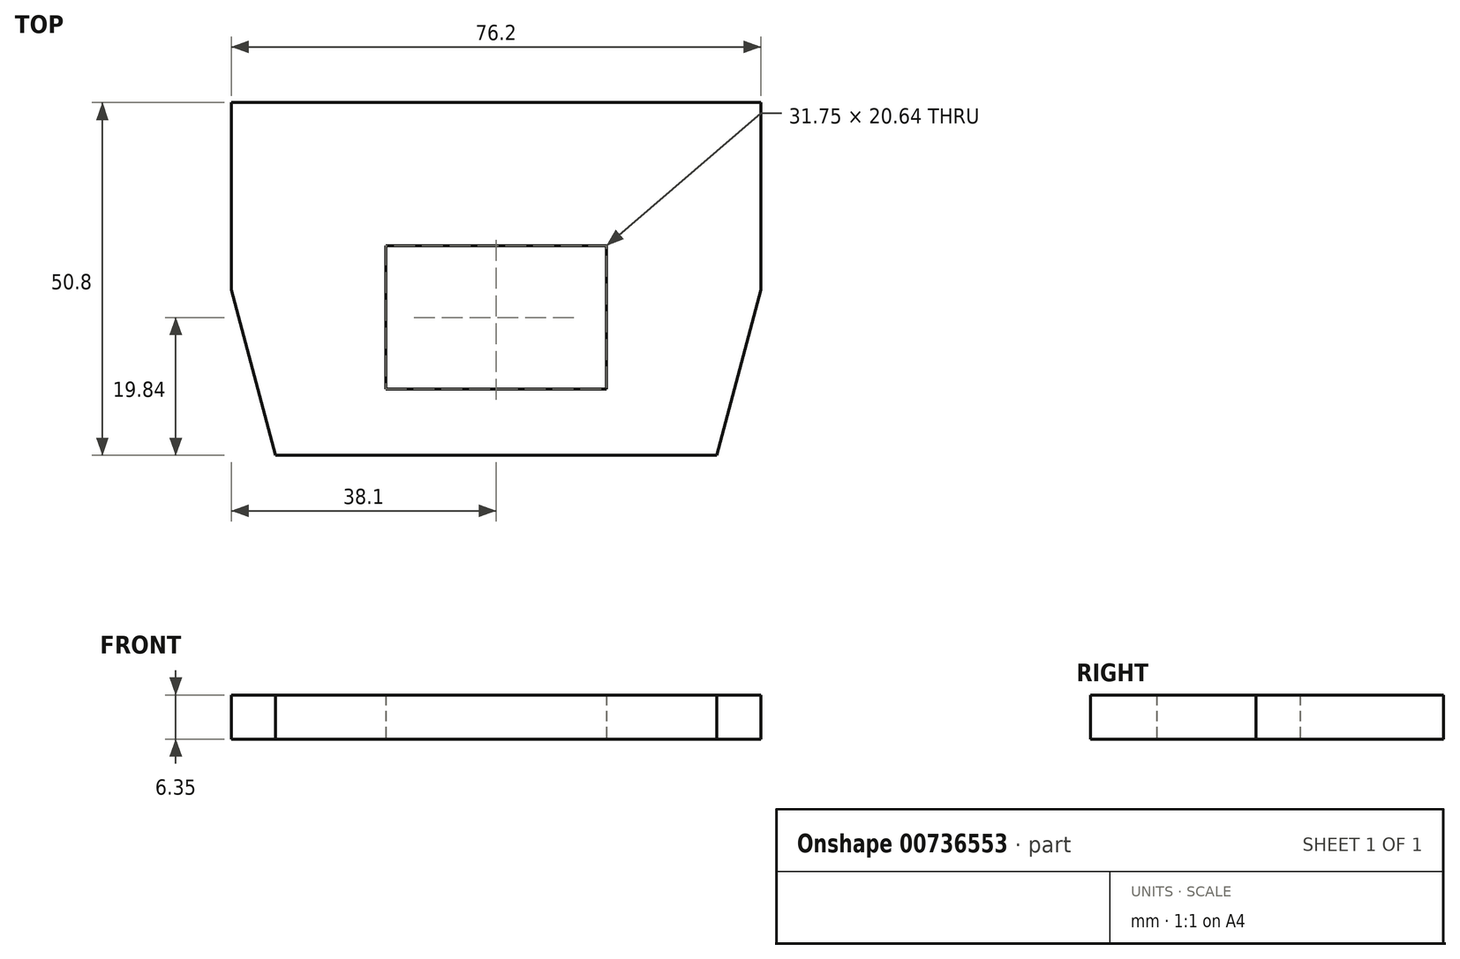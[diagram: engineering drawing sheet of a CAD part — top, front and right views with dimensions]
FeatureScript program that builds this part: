
annotation { "Feature Type Name" : "Feature", "Feature Type Description" : "" }
export const myFeature = defineFeature(function(context is Context, id is Id, definition is map)
    precondition{}
    {
        {
            var Q0;
            Q0=qCreatedBy(makeId("Top.planeOp"),FACE);
            var sketch = newSketch(context, id + "F0", { "sketchPlane" : qUnion([Q0])});
            skLineSegment(sketch, "E0", {"start": v(-75.44, 0) * mm, "end": v(76.77, 0) * mm, "construction": true});
            skLineSegment(sketch, "E1", {"start": v(0, 73.43) * mm, "end": v(0, -67) * mm, "construction": true});
            skLineSegment(sketch, "E2.0", {"start": v(38.1, 30.96) * mm, "end": v(38.1, 3.97) * mm});
            skLineSegment(sketch, "E3.0", {"start": v(0, 10.32) * mm, "end": v(15.88, 10.32) * mm});
            skLineSegment(sketch, "E4.0", {"start": v(0, -10.32) * mm, "end": v(15.88, -10.32) * mm});
            skLineSegment(sketch, "E5.0", {"start": v(0, -19.84) * mm, "end": v(31.75, -19.84) * mm});
            skLineSegment(sketch, "E6.0", {"start": v(0, 30.96) * mm, "end": v(38.1, 30.96) * mm});
            skLineSegment(sketch, "E7.0", {"start": v(-75.44, 3.97) * mm, "end": v(76.77, 3.97) * mm, "construction": true});
            skLineSegment(sketch, "E8", {"start": v(31.75, -19.84) * mm, "end": v(38.1, 3.97) * mm});
            skLineSegment(sketch, "E9.trimOffspring", {"start": v(15.88, 10.32) * mm, "end": v(15.88, -10.32) * mm});
            skLineSegment(sketch, "E10.MirrorCS", {"start": v(0, 30.96) * mm, "end": v(-38.1, 30.96) * mm});
            skLineSegment(sketch, "E11.MirrorCS", {"start": v(-38.1, 30.96) * mm, "end": v(-38.1, 3.97) * mm});
            skLineSegment(sketch, "E12.MirrorCS", {"start": v(-31.75, -19.84) * mm, "end": v(-38.1, 3.97) * mm});
            skLineSegment(sketch, "E13.MirrorCS", {"start": v(0, -19.84) * mm, "end": v(-31.75, -19.84) * mm});
            skLineSegment(sketch, "E14.MirrorCS", {"start": v(0, -10.32) * mm, "end": v(-15.88, -10.32) * mm});
            skLineSegment(sketch, "E15.MirrorCS", {"start": v(-15.88, 10.32) * mm, "end": v(-15.88, -10.32) * mm});
            skLineSegment(sketch, "E16.MirrorCS", {"start": v(0, 10.32) * mm, "end": v(-15.88, 10.32) * mm});
            skSolve(sketch);
        }
        {
            var Q0;
            Q0=makeQuery(id+"F0.imprint","IMPRINT",FACE,{"disambiguationData":[TD([[makeQuery(id+"F0.imprint","IMPRINT",EDGE,{"derivedFrom":sQuery(id+"F0.wireOp",EDGE,"E2.0")}),-1.0]])]});
            extrude(context, id + "F1", {"entities" : qUnion([Q0]), "depth" : 6.35 * mm, "offsetDistance" : 25.4 * mm});
        }
    });
